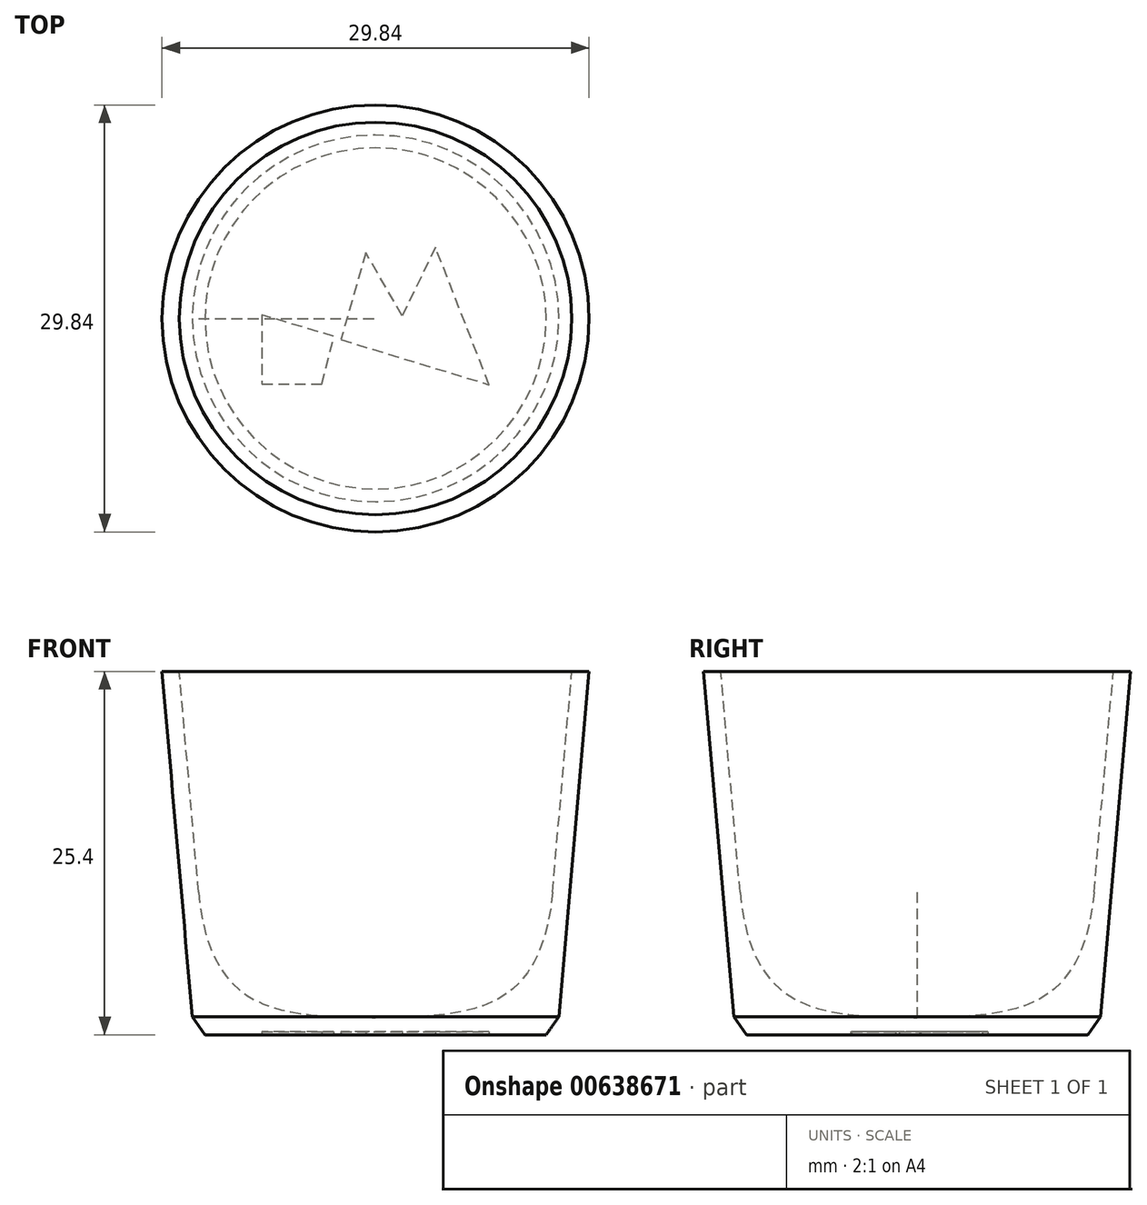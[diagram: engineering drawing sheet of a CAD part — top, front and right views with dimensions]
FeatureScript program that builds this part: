
annotation { "Feature Type Name" : "Feature", "Feature Type Description" : "" }
export const myFeature = defineFeature(function(context is Context, id is Id, definition is map)
    precondition{}
    {
        {
            var Q0;
            Q0=qCreatedBy(makeId("Front.planeOp"),FACE);
            var sketch = newSketch(context, id + "F0", { "sketchPlane" : qUnion([Q0])});
            skLineSegment(sketch, "E0", {"start": v(0, 0) * mm, "end": v(0, 25.4) * mm});
            skLineSegment(sketch, "E1", {"start": v(0, 25.4) * mm, "end": v(-14.92, 25.4) * mm});
            skLineSegment(sketch, "E2", {"start": v(-14.92, 25.4) * mm, "end": v(-12.7, 0) * mm});
            skLineSegment(sketch, "E3", {"start": v(-12.7, 0) * mm, "end": v(0, 0) * mm});
            skLineSegment(sketch, "E4", {"start": v(-13.72, 25.4) * mm, "end": v(-12.37, 9.97) * mm});
            skFitSpline(sketch, "E5", {"points": [v(-12.37, 9.97) * mm, v(0, 1.2) * mm], "startDerivative": vector(2.35, -26.88) * mm, "endDerivative": vector(18, -0.5) * mm});
            skLineSegment(sketch, "E6", {"start": v(-12.37, 9.97) * mm, "end": v(-11.58, 1) * mm, "construction": true});
            skSolve(sketch);
        }
        {
            var Q0;
            {var subQ0=sQuery(id+"F0.wireOp",EDGE,"E2");Q0=makeQuery(id+"F0.imprint","IMPRINT",FACE,{"disambiguationData":[TD([[makeQuery(id+"F0.imprint","IMPRINT",EDGE,{"derivedFrom":subQ0}),1.0]])]});}
            var Q1;
            Q1=sQuery(id+"F0.wireOp",EDGE,"E0");
            revolve(context, id + "F1", {"entities" : qUnion([Q0]), "axis" : qUnion([Q1]), "revolveType" : RevolveType.FULL});
        }
        {
            var Q0;
            Q0=makeQuery(id+"F1.opRevolve","SWEPT_EDGE",EDGE,{"disambiguationData":[OSD([sQuery(id+"F0.wireOp",EDGE,"E2"),sQuery(id+"F0.wireOp",EDGE,"E3")])]});
            chamfer(context, id + "F2", {"entities" : qUnion([Q0]), "chamferType" : ChamferType.OFFSET_ANGLE, "width" : 1.27 * mm, "oppositeDirection" : true, "angle" : 30 * degree, "tangentPropagation" : true});
        }
        {
            var Q0;
            Q0=qCreatedBy(makeId("Top.planeOp"),FACE);
            var sketch = newSketch(context, id + "F3", { "sketchPlane" : qUnion([Q0])});
            skLineSegment(sketch, "E7.MirrorCS", {"start": v(-7.94, -4.58) * mm, "end": v(-3.75, -4.58) * mm});
            skLineSegment(sketch, "E8.MirrorCS", {"start": v(-7.94, 0.25) * mm, "end": v(-7.94, -4.58) * mm});
            skLineSegment(sketch, "E9.MirrorCS", {"start": v(-2.92, -1.26) * mm, "end": v(-7.94, 0.25) * mm});
            skLineSegment(sketch, "E10.MirrorCS", {"start": v(-2.42, -1.49) * mm, "end": v(7.94, -4.63) * mm});
            skLineSegment(sketch, "E11.MirrorCS", {"start": v(1.86, 0.19) * mm, "end": v(-0.68, 4.58) * mm});
            skLineSegment(sketch, "E12.MirrorCS", {"start": v(4.2, 4.96) * mm, "end": v(1.86, 0.19) * mm});
            skLineSegment(sketch, "E13.MirrorCS", {"start": v(-3.75, -4.58) * mm, "end": v(-2.92, -1.26) * mm});
            skLineSegment(sketch, "E14.MirrorCS", {"start": v(-0.68, 4.58) * mm, "end": v(-2.42, -1.49) * mm});
            skLineSegment(sketch, "E15.MirrorCS", {"start": v(7.94, -4.63) * mm, "end": v(4.2, 4.96) * mm});
            skLineSegment(sketch, "E16.bottom", {"start": v(7.94, 4.58) * mm, "end": v(-7.94, 4.58) * mm, "construction": true});
            skLineSegment(sketch, "E16.top", {"start": v(7.94, -4.58) * mm, "end": v(-7.94, -4.58) * mm, "construction": true});
            skLineSegment(sketch, "E16.left", {"start": v(7.94, 4.58) * mm, "end": v(7.94, -4.58) * mm, "construction": true});
            skLineSegment(sketch, "E16.right", {"start": v(-7.94, 4.58) * mm, "end": v(-7.94, -4.58) * mm, "construction": true});
            skLineSegment(sketch, "E17", {"start": v(0, 0) * mm, "end": v(0, 4.58) * mm, "construction": true});
            skLineSegment(sketch, "E18", {"start": v(0, 0) * mm, "end": v(7.94, 0) * mm, "construction": true});
            skSolve(sketch);
        }
        {
            var Q0;
            Q0 = qSketchRegion(id + "F3", true);
            extrude(context, id + "F4", {"entities" : qUnion([Q0]), "operationType" : NewBodyOperationType.REMOVE, "depth" : 0.2 * mm, "offsetDistance" : 25.4 * mm});
        }
        {
            var Q0;
            {var subQ4=sQuery(id+"F0.wireOp",EDGE,"E4");Q0=makeQuery(id+"F0.imprint","IMPRINT",FACE,{"disambiguationData":[TD([[makeQuery(id+"F0.imprint","IMPRINT",EDGE,{"derivedFrom":subQ4}),1.0]])]});}
            var Q1;
            Q1=sQuery(id+"F0.wireOp",EDGE,"E0");
            revolve(context, id + "F5", {"entities" : qUnion([Q0]), "axis" : qUnion([Q1]), "revolveType" : RevolveType.FULL});
        }
    });
